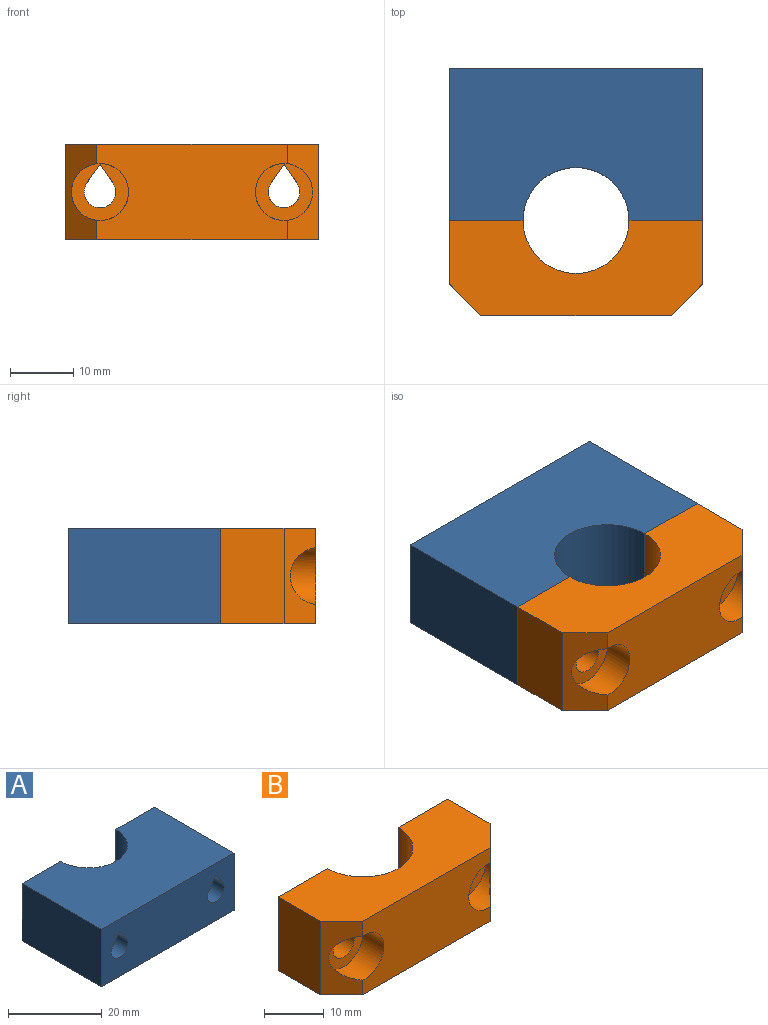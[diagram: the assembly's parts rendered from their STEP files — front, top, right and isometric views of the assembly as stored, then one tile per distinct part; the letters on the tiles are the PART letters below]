
ASSEMBLY  parts=2 mates=1
PART A: 16 faces, bbox 40x24x15 mm
  f0: plane 15x11.65mm, normal (0,1,0), area 152.2mm2, adj f1,f5,f6,f7,f12,f13,f14,f15
  f1: cylinder r=8.35mm len=16.7mm, axis (0,0,-1), area 393.5mm2, adj f0,f2,f6,f7
  f2: plane 15x11.65mm, normal (0,1,0), area 152.2mm2, adj f1,f3,f6,f7,f8,f9,f10,f11
  f3: plane 24x15mm, normal (-1,0,0), area 360mm2, adj f2,f4,f6,f7
  f4: plane 40x15mm, normal (0,-1,0), area 554.9mm2, adj f3,f5,f6,f7,f8,f9,f10,f11
  f5: plane 24x15mm, normal (1,0,0), area 360mm2, adj f0,f4,f6,f7
  f6: plane 40x24mm, normal (0,0,1), area 850.5mm2, adj f0,f1,f2,f3,f4,f5
  f7: plane 40x24mm, normal (0,0,-1), area 850.5mm2, adj f0,f1,f2,f3,f4,f5
  f8: plane 24x0mm, normal (0,0,1), area 0.1mm2, adj f2,f4,f9,f11
  f9: cylinder r=2.5mm len=24mm, axis (0,1,0), area 263.7mm2, adj f2,f4,f8,f10
  f10: plane 24x2.81mm, normal (0.82,0,-0.57), area 82.4mm2, adj f2,f4,f9,f11
  f11: plane 24x2.96mm, normal (-0.82,0,-0.58), area 86.8mm2, adj f2,f4,f8,f10
  f12: plane 24x0mm, normal (0,0,1), area 0.1mm2, adj f0,f4,f13,f15
  f13: cylinder r=2.5mm len=24mm, axis (0,1,0), area 263.7mm2, adj f0,f4,f12,f14
  f14: plane 24x2.81mm, normal (0.82,0,-0.57), area 82.4mm2, adj f0,f4,f13,f15
  f15: plane 24x2.96mm, normal (-0.82,0,-0.58), area 86.8mm2, adj f0,f4,f12,f14
PART B: 21 faces, bbox 40x15x15 mm
  f0: cylinder r=2.5mm len=10mm, axis (0,1,0), area 109.1mm2, adj f1,f3,f9,f17
  f1: plane 10x0.04mm, normal (0,0,1), area 0.4mm2, adj f0,f2,f9,f17
  f2: plane 10x2.93mm, normal (0.81,0,-0.58), area 36.1mm2, adj f1,f3,f9,f17
  f3: plane 10x2.9mm, normal (-0.82,0,-0.57), area 35.4mm2, adj f0,f2,f9,f17
  f4: cylinder r=2.5mm len=10mm, axis (0,1,0), area 109.8mm2, adj f5,f6,f7,f19
  f5: plane 10x2.89mm, normal (0.82,0,-0.58), area 35.3mm2, adj f4,f6,f7,f19
  f6: plane 10x2.89mm, normal (-0.82,0,-0.57), area 35.3mm2, adj f4,f5,f7,f19
  f7: plane 15x11.65mm, normal (0,1,0), area 152.2mm2, adj f4,f5,f6,f8,f12,f13,f14
  f8: cylinder r=8.35mm len=16.7mm, axis (0,0,1), area 393.5mm2, adj f7,f9,f13,f14
  f9: plane 15x11.65mm, normal (0,1,0), area 152.2mm2, adj f0,f1,f2,f3,f8,f10,f13,f14
  f10: plane 15x10mm, normal (-1,0,0), area 150mm2, adj f9,f13,f14,f16
  f11: plane 30x15mm, normal (0,-1,0), area 377.4mm2, adj f13,f14,f15,f16,f18,f20
  f12: plane 15x10mm, normal (1,0,0), area 150mm2, adj f7,f13,f14,f15
  f13: plane 40x15mm, normal (0,0,-1), area 465.5mm2, adj f7,f8,f9,f10,f11,f12,f15,f16
  f14: plane 40x15mm, normal (0,0,1), area 465.5mm2, adj f7,f8,f9,f10,f11,f12,f15,f16
  f15: plane 15x5mm, normal (0.71,-0.71,0), area 67.4mm2, adj f11,f12,f13,f14,f20
  f16: plane 15x5mm, normal (-0.71,-0.71,0), area 67.4mm2, adj f10,f11,f13,f14,f18
  f17: plane 9x9mm, normal (0,-1,0), area 41mm2, adj f0,f1,f2,f3,f18
  f18: cylinder r=4.5mm len=9mm, axis (0,-1,0), area 107.7mm2, adj f11,f16,f17
  f19: plane 9x9mm, normal (0,-1,0), area 41.1mm2, adj f4,f5,f6,f20
  f20: cylinder r=4.5mm len=9mm, axis (0,-1,0), area 107.7mm2, adj f11,f15,f19
PLACE A rot(axis=(0,0,1),180deg) t=(-1.27,21.62,-15)mm
PLACE B t=(-1.5,0,0)mm
MATE fastened A.f6 <-> B.f14  axis (0,0,1) through (-9.85,3.76,0)mm
